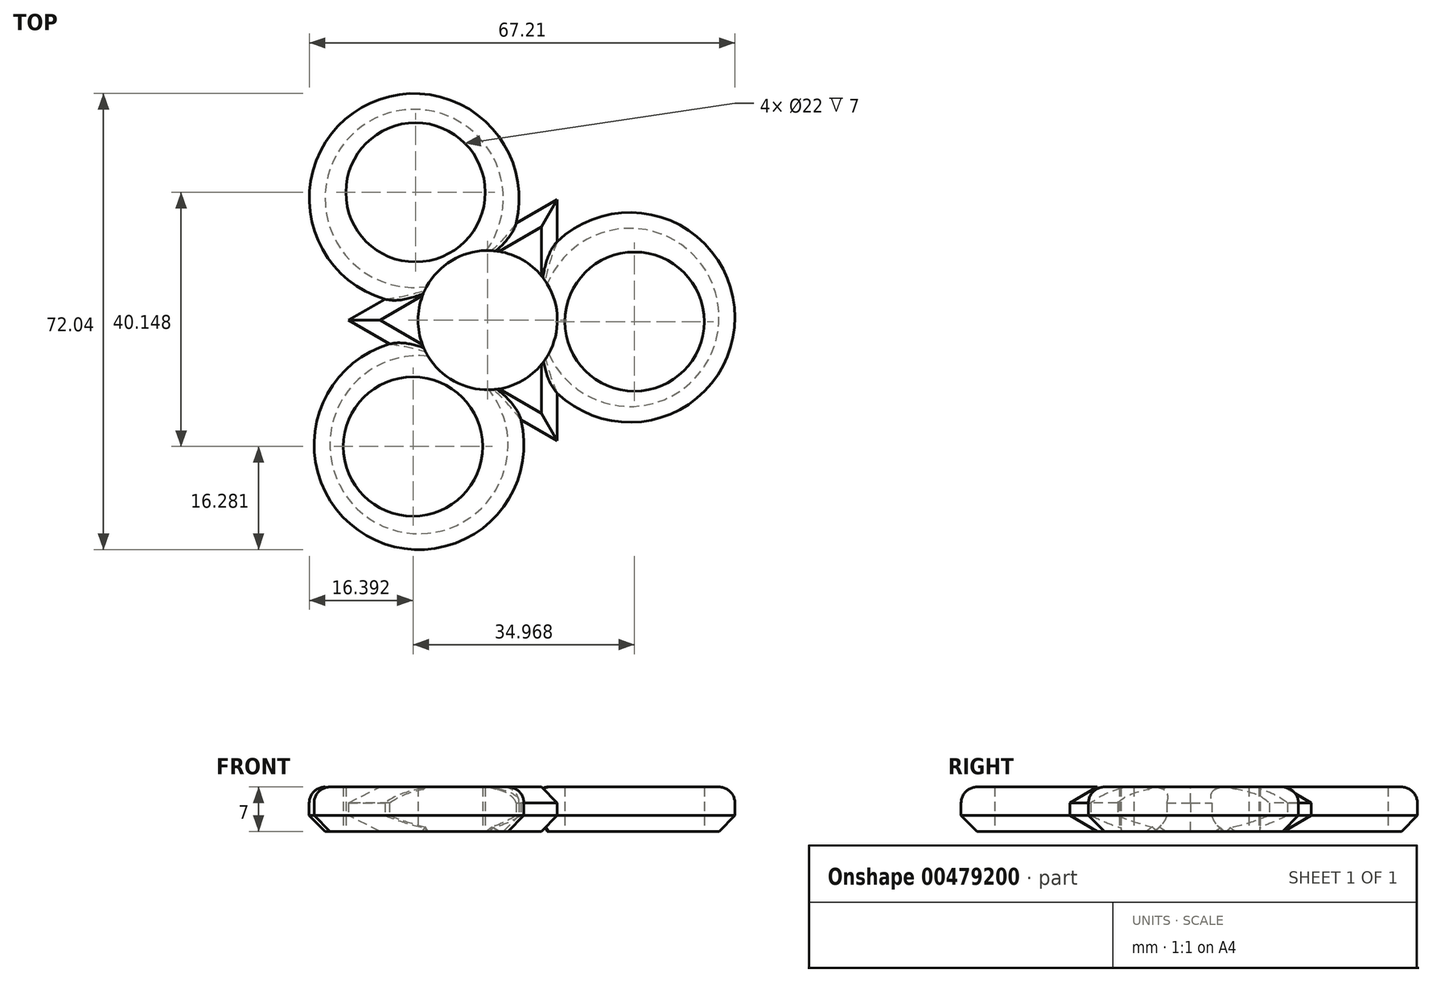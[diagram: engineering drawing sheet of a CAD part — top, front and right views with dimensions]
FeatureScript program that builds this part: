
annotation { "Feature Type Name" : "Feature", "Feature Type Description" : "" }
export const myFeature = defineFeature(function(context is Context, id is Id, definition is map)
    precondition{}
    {
        {
            var Q0;
            Q0=qCreatedBy(makeId("Top.planeOp"),FACE);
            var sketch = newSketch(context, id + "F0", { "sketchPlane" : qUnion([Q0])});
            skCircle(sketch, "E0", {"center": v(0, 0) * mm, "radius": 11 * mm});
            skCircle(sketch, "E1.cCircle", {"center": v(0, 0) * mm, "radius": 11 * mm, "construction": true});
            skLineSegment(sketch, "E1.0", {"start": v(11, 19.05) * mm, "end": v(11, -19.05) * mm});
            skLineSegment(sketch, "E1.1", {"start": v(11, -19.05) * mm, "end": v(-22, 0) * mm});
            skLineSegment(sketch, "E1.2", {"start": v(-22, 0) * mm, "end": v(11, 19.05) * mm});
            skPoint(sketch, "E1.0.midPoint", {"position": v(11, 0) * mm});
            skCircle(sketch, "E2", {"center": v(-11.4, 20.19) * mm, "radius": 11 * mm});
            skCircle(sketch, "E3.1.0", {"center": v(-11.79, -19.96) * mm, "radius": 11 * mm});
            skCircle(sketch, "E3.2.0", {"center": v(23.18, -0.23) * mm, "radius": 11 * mm});
            skArc(sketch, "E4", {"start": v(4.48, 15.29) * mm, "mid": v(-19.9, 33.58) * mm, "end": v(-16.24, 3.32) * mm});
            skArc(sketch, "E5.1.0", {"start": v(-15.48, -3.77) * mm, "mid": v(-19.13, -34.02) * mm, "end": v(5.24, -15.73) * mm});
            skArc(sketch, "E5.2.0", {"start": v(11, -11.52) * mm, "mid": v(39.03, 0.44) * mm, "end": v(11, 12.4) * mm});
            skSolve(sketch);
        }
        {
            var Q0;
            {var subQ0=sQuery(id+"F0.wireOp",EDGE,"E1.2");var subQ4=sQuery(id+"F0.wireOp",EDGE,"E0");var subQ7=makeQuery(id+"F0.imprint","INTERSECT",VERTEX,{"derivedFrom":[subQ4,subQ0]});Q0=makeQuery(id+"F0.imprint","IMPRINT",FACE,{"disambiguationData":[TD([[makeQuery(id+"F0.imprint","IMPRINT",EDGE,{"disambiguationData":[TD([[subQ7,-1.0]])],"derivedFrom":subQ4}),-1.0]])]});}
            var Q1;
            Q1=makeQuery(id+"F0.imprint","IMPRINT",FACE,{"disambiguationData":[TD([[makeQuery(id+"F0.imprint","IMPRINT",EDGE,{"derivedFrom":sQuery(id+"F0.wireOp",EDGE,"E3.1.0")}),-1.0]])]});
            var Q2;
            {var subQ1=sQuery(id+"F0.wireOp",EDGE,"E1.0");var subQ4=sQuery(id+"F0.wireOp",EDGE,"E0");var subQ5=makeQuery(id+"F0.imprint","INTERSECT",VERTEX,{"derivedFrom":[subQ4,subQ1]});Q2=makeQuery(id+"F0.imprint","IMPRINT",FACE,{"disambiguationData":[TD([[makeQuery(id+"F0.imprint","IMPRINT",EDGE,{"disambiguationData":[TD([[subQ5,1.0]])],"derivedFrom":subQ4}),-1.0]])]});}
            var Q3;
            {var subQ2=sQuery(id+"F0.wireOp",EDGE,"E0");var subQ4=sQuery(id+"F0.wireOp",EDGE,"E1.2");var subQ6=makeQuery(id+"F0.imprint","INTERSECT",VERTEX,{"derivedFrom":[subQ2,subQ4]});Q3=makeQuery(id+"F0.imprint","IMPRINT",FACE,{"disambiguationData":[TD([[makeQuery(id+"F0.imprint","IMPRINT",EDGE,{"disambiguationData":[TD([[subQ6,1.0]])],"derivedFrom":subQ2}),-1.0]])]});}
            var Q4;
            Q4=makeQuery(id+"F0.imprint","IMPRINT",FACE,{"disambiguationData":[TD([[makeQuery(id+"F0.imprint","IMPRINT",EDGE,{"derivedFrom":sQuery(id+"F0.wireOp",EDGE,"E3.2.0")}),-1.0]])]});
            var Q5;
            Q5=makeQuery(id+"F0.imprint","IMPRINT",FACE,{"disambiguationData":[TD([[makeQuery(id+"F0.imprint","IMPRINT",EDGE,{"derivedFrom":sQuery(id+"F0.wireOp",EDGE,"E2")}),-1.0]])]});
            extrude(context, id + "F1", {"entities" : qUnion([Q0, Q1, Q2, Q3, Q4, Q5]), "depth" : 7 * mm});
        }
        {
            var Q0;
            {var subQ0=sQuery(id+"F0.wireOp",EDGE,"E1.1");Q0=makeQuery(id+"F1.opExtrude","CAP_EDGE",EDGE,{"disambiguationData":[OSD([subQ0]),TDD([makeQuery(id+"F0.imprint","IMPRINT",EDGE,{"disambiguationData":[TD([[makeQuery(id+"F0.imprint","INTERSECT",VERTEX,{"derivedFrom":[subQ0,sQuery(id+"F0.wireOp",EDGE,"E1.2")]}),1.0]])],"derivedFrom":subQ0})])],"isStart":false});}
            var Q1;
            {var subQ0=sQuery(id+"F0.wireOp",EDGE,"E1.2");Q1=makeQuery(id+"F1.opExtrude","CAP_EDGE",EDGE,{"disambiguationData":[OSD([subQ0]),TDD([makeQuery(id+"F0.imprint","IMPRINT",EDGE,{"disambiguationData":[TD([[makeQuery(id+"F0.imprint","INTERSECT",VERTEX,{"derivedFrom":[sQuery(id+"F0.wireOp",EDGE,"E1.1"),subQ0]}),-1.0]])],"derivedFrom":subQ0})])],"isStart":false});}
            var Q2;
            {var subQ0=sQuery(id+"F0.wireOp",EDGE,"E1.1");Q2=makeQuery(id+"F1.opExtrude","CAP_EDGE",EDGE,{"disambiguationData":[OSD([subQ0]),TDD([makeQuery(id+"F0.imprint","IMPRINT",EDGE,{"disambiguationData":[TD([[makeQuery(id+"F0.imprint","INTERSECT",VERTEX,{"derivedFrom":[subQ0,sQuery(id+"F0.wireOp",EDGE,"E1.2")]}),1.0]])],"derivedFrom":subQ0})])],"isStart":true});}
            var Q3;
            {var subQ0=sQuery(id+"F0.wireOp",EDGE,"E1.2");Q3=makeQuery(id+"F1.opExtrude","CAP_EDGE",EDGE,{"disambiguationData":[OSD([subQ0]),TDD([makeQuery(id+"F0.imprint","IMPRINT",EDGE,{"disambiguationData":[TD([[makeQuery(id+"F0.imprint","INTERSECT",VERTEX,{"derivedFrom":[sQuery(id+"F0.wireOp",EDGE,"E1.1"),subQ0]}),-1.0]])],"derivedFrom":subQ0})])],"isStart":true});}
            var Q4;
            {var subQ0=sQuery(id+"F0.wireOp",EDGE,"E1.1");Q4=makeQuery(id+"F1.opExtrude","CAP_EDGE",EDGE,{"disambiguationData":[OSD([subQ0]),TDD([makeQuery(id+"F0.imprint","IMPRINT",EDGE,{"disambiguationData":[TD([[makeQuery(id+"F0.imprint","INTERSECT",VERTEX,{"derivedFrom":[sQuery(id+"F0.wireOp",EDGE,"E1.0"),subQ0]}),-1.0]])],"derivedFrom":subQ0})])],"isStart":false});}
            var Q5;
            {var subQ0=sQuery(id+"F0.wireOp",EDGE,"E1.0");Q5=makeQuery(id+"F1.opExtrude","CAP_EDGE",EDGE,{"disambiguationData":[OSD([subQ0]),TDD([makeQuery(id+"F0.imprint","IMPRINT",EDGE,{"disambiguationData":[TD([[makeQuery(id+"F0.imprint","INTERSECT",VERTEX,{"derivedFrom":[subQ0,sQuery(id+"F0.wireOp",EDGE,"E1.1")]}),1.0]])],"derivedFrom":subQ0})])],"isStart":false});}
            var Q6;
            {var subQ0=sQuery(id+"F0.wireOp",EDGE,"E1.1");Q6=makeQuery(id+"F1.opExtrude","CAP_EDGE",EDGE,{"disambiguationData":[OSD([subQ0]),TDD([makeQuery(id+"F0.imprint","IMPRINT",EDGE,{"disambiguationData":[TD([[makeQuery(id+"F0.imprint","INTERSECT",VERTEX,{"derivedFrom":[sQuery(id+"F0.wireOp",EDGE,"E1.0"),subQ0]}),-1.0]])],"derivedFrom":subQ0})])],"isStart":true});}
            var Q7;
            {var subQ0=sQuery(id+"F0.wireOp",EDGE,"E1.0");Q7=makeQuery(id+"F1.opExtrude","CAP_EDGE",EDGE,{"disambiguationData":[OSD([subQ0]),TDD([makeQuery(id+"F0.imprint","IMPRINT",EDGE,{"disambiguationData":[TD([[makeQuery(id+"F0.imprint","INTERSECT",VERTEX,{"derivedFrom":[subQ0,sQuery(id+"F0.wireOp",EDGE,"E1.1")]}),1.0]])],"derivedFrom":subQ0})])],"isStart":true});}
            var Q8;
            {var subQ0=sQuery(id+"F0.wireOp",EDGE,"E1.0");Q8=makeQuery(id+"F1.opExtrude","CAP_EDGE",EDGE,{"disambiguationData":[OSD([subQ0]),TDD([makeQuery(id+"F0.imprint","IMPRINT",EDGE,{"disambiguationData":[TD([[makeQuery(id+"F0.imprint","INTERSECT",VERTEX,{"derivedFrom":[subQ0,sQuery(id+"F0.wireOp",EDGE,"E1.2")]}),-1.0]])],"derivedFrom":subQ0})])],"isStart":false});}
            var Q9;
            {var subQ0=sQuery(id+"F0.wireOp",EDGE,"E1.0");Q9=makeQuery(id+"F1.opExtrude","CAP_EDGE",EDGE,{"disambiguationData":[OSD([subQ0]),TDD([makeQuery(id+"F0.imprint","IMPRINT",EDGE,{"disambiguationData":[TD([[makeQuery(id+"F0.imprint","INTERSECT",VERTEX,{"derivedFrom":[subQ0,sQuery(id+"F0.wireOp",EDGE,"E1.2")]}),-1.0]])],"derivedFrom":subQ0})])],"isStart":true});}
            var Q10;
            {var subQ0=sQuery(id+"F0.wireOp",EDGE,"E1.2");Q10=makeQuery(id+"F1.opExtrude","CAP_EDGE",EDGE,{"disambiguationData":[OSD([subQ0]),TDD([makeQuery(id+"F0.imprint","IMPRINT",EDGE,{"disambiguationData":[TD([[makeQuery(id+"F0.imprint","INTERSECT",VERTEX,{"derivedFrom":[sQuery(id+"F0.wireOp",EDGE,"E1.0"),subQ0]}),1.0]])],"derivedFrom":subQ0})])],"isStart":false});}
            var Q11;
            {var subQ0=sQuery(id+"F0.wireOp",EDGE,"E1.2");Q11=makeQuery(id+"F1.opExtrude","CAP_EDGE",EDGE,{"disambiguationData":[OSD([subQ0]),TDD([makeQuery(id+"F0.imprint","IMPRINT",EDGE,{"disambiguationData":[TD([[makeQuery(id+"F0.imprint","INTERSECT",VERTEX,{"derivedFrom":[sQuery(id+"F0.wireOp",EDGE,"E1.0"),subQ0]}),1.0]])],"derivedFrom":subQ0})])],"isStart":true});}
            var Q12;
            Q12=makeQuery(id+"F1.opExtrude","CAP_EDGE",EDGE,{"disambiguationData":[OSD([sQuery(id+"F0.wireOp",EDGE,"E5.2.0")])],"isStart":true});
            var Q13;
            Q13=makeQuery(id+"F1.opExtrude","CAP_EDGE",EDGE,{"disambiguationData":[OSD([sQuery(id+"F0.wireOp",EDGE,"E4")])],"isStart":true});
            var Q14;
            Q14=makeQuery(id+"F1.opExtrude","CAP_EDGE",EDGE,{"disambiguationData":[OSD([sQuery(id+"F0.wireOp",EDGE,"E5.1.0")])],"isStart":true});
            chamfer(context, id + "F2", {"entities" : qUnion([Q0, Q1, Q2, Q3, Q4, Q5, Q6, Q7, Q8, Q9, Q10, Q11, Q12, Q13, Q14]), "width" : 2.5 * mm, "tangentPropagation" : true});
        }
        {
            var Q0;
            Q0=makeQuery(id+"F1.opExtrude","CAP_EDGE",EDGE,{"disambiguationData":[OSD([sQuery(id+"F0.wireOp",EDGE,"E5.1.0")])],"isStart":false});
            var Q1;
            Q1=makeQuery(id+"F1.opExtrude","CAP_EDGE",EDGE,{"disambiguationData":[OSD([sQuery(id+"F0.wireOp",EDGE,"E5.2.0")])],"isStart":false});
            var Q2;
            Q2=makeQuery(id+"F1.opExtrude","CAP_EDGE",EDGE,{"disambiguationData":[OSD([sQuery(id+"F0.wireOp",EDGE,"E4")])],"isStart":false});
            fillet(context, id + "F3", {"entities" : qUnion([Q0, Q1, Q2]), "radius" : 2.5 * mm, "tangentPropagation" : true, "allowEdgeOverflow" : false});
        }
    });
